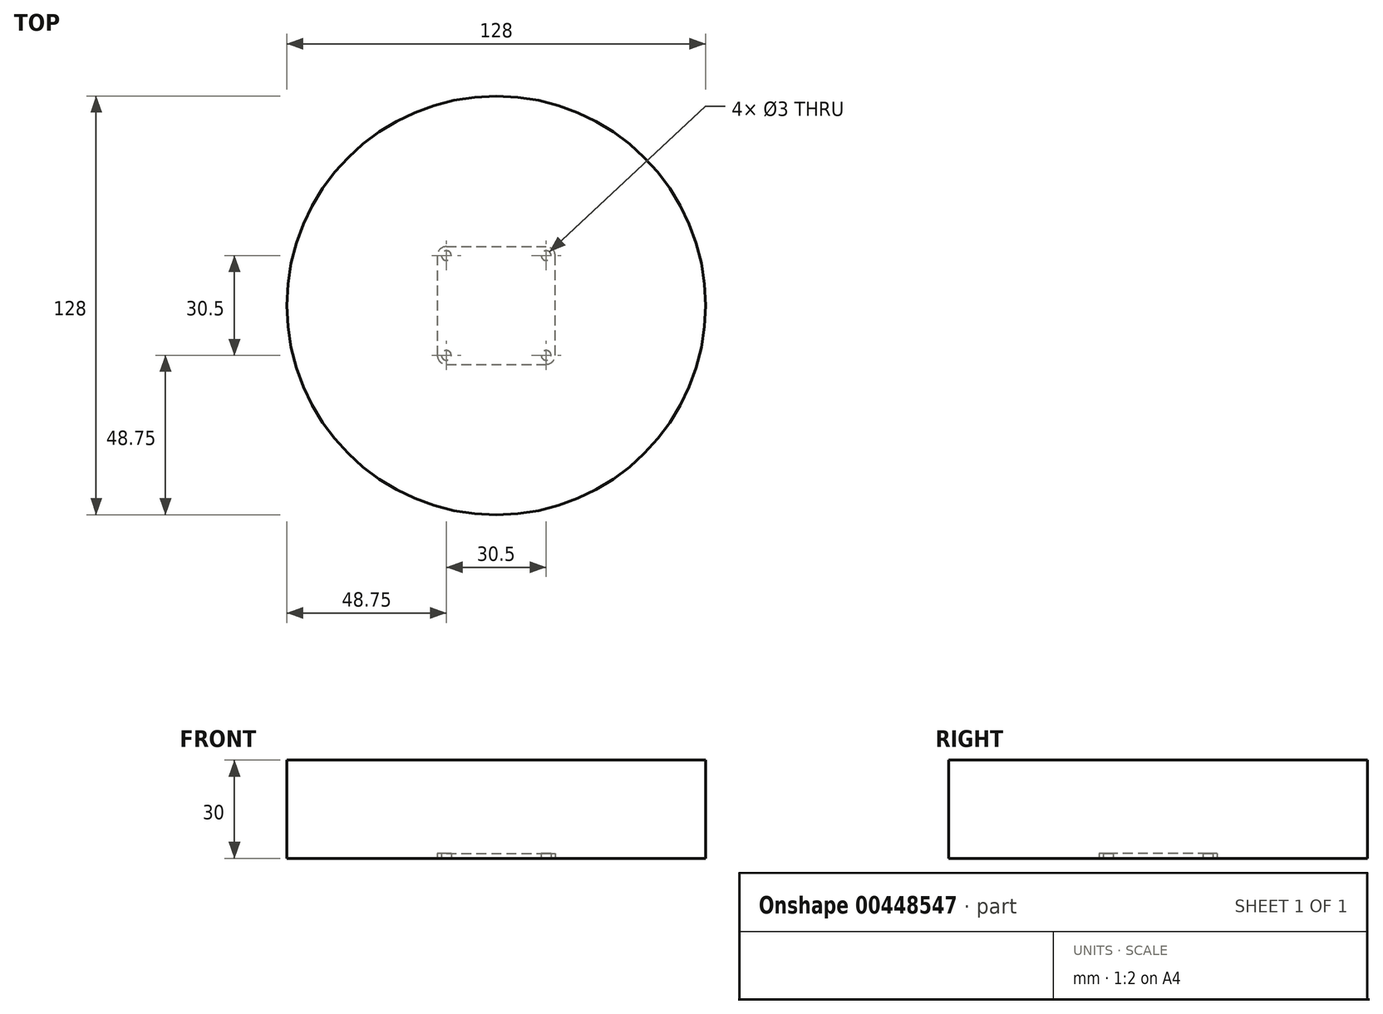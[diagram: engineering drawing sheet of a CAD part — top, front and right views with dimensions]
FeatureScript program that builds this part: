
annotation { "Feature Type Name" : "Feature", "Feature Type Description" : "" }
export const myFeature = defineFeature(function(context is Context, id is Id, definition is map)
    precondition{}
    {
        {
            var Q0;
            Q0=qCreatedBy(makeId("Top.planeOp"),FACE);
            var sketch = newSketch(context, id + "F0", { "sketchPlane" : qUnion([Q0])});
            skLineSegment(sketch, "E0.bottom", {"start": v(-15.25, 18) * mm, "end": v(0, 18) * mm});
            skLineSegment(sketch, "E0.left", {"start": v(-18, 15.25) * mm, "end": v(-18, 0) * mm});
            skCircle(sketch, "E1", {"center": v(-15.25, 15.25) * mm, "radius": 1.5 * mm});
            skLineSegment(sketch, "E2", {"start": v(0, 0) * mm, "end": v(0, 18) * mm, "construction": true});
            skLineSegment(sketch, "E3", {"start": v(0, 0) * mm, "end": v(-18, 0) * mm, "construction": true});
            skPoint(sketch, "E4.visualSharp", {"position": v(-18, 18) * mm});
            skArc(sketch, "E4.filletArc", {"start": v(-15.25, 18) * mm, "mid": v(-17.2, 17.2) * mm, "end": v(-18, 15.25) * mm});
            skCircle(sketch, "E5.MirrorC", {"center": v(15.25, 15.25) * mm, "radius": 1.5 * mm});
            skArc(sketch, "E6.MirrorCS", {"start": v(15.25, 18) * mm, "mid": v(17.2, 17.2) * mm, "end": v(18, 15.25) * mm});
            skPoint(sketch, "E7.MirrorP", {"position": v(18, 18) * mm});
            skLineSegment(sketch, "E8.MirrorCS", {"start": v(18, 15.25) * mm, "end": v(18, 0) * mm});
            skLineSegment(sketch, "E9.MirrorCS", {"start": v(15.25, 18) * mm, "end": v(0, 18) * mm});
            skLineSegment(sketch, "E10.MirrorCS", {"start": v(18, -15.25) * mm, "end": v(18, 0) * mm});
            skLineSegment(sketch, "E11.MirrorCS", {"start": v(-18, -15.25) * mm, "end": v(-18, 0) * mm});
            skArc(sketch, "E12.MirrorCS", {"start": v(-15.25, -18) * mm, "mid": v(-17.2, -17.2) * mm, "end": v(-18, -15.25) * mm});
            skArc(sketch, "E13.MirrorCS", {"start": v(15.25, -18) * mm, "mid": v(17.2, -17.2) * mm, "end": v(18, -15.25) * mm});
            skLineSegment(sketch, "E14.MirrorCS", {"start": v(-15.25, -18) * mm, "end": v(0, -18) * mm});
            skPoint(sketch, "E15.MirrorP", {"position": v(18, -18) * mm});
            skPoint(sketch, "E16.MirrorP", {"position": v(-18, -18) * mm});
            skCircle(sketch, "E17.MirrorC", {"center": v(-15.25, -15.25) * mm, "radius": 1.5 * mm});
            skCircle(sketch, "E18.MirrorC", {"center": v(15.25, -15.25) * mm, "radius": 1.5 * mm});
            skLineSegment(sketch, "E19.MirrorCS", {"start": v(15.25, -18) * mm, "end": v(0, -18) * mm});
            skSolve(sketch);
        }
        {
            var Q0;
            Q0=makeQuery(id+"F0.imprint","IMPRINT",FACE,{"disambiguationData":[TD([[makeQuery(id+"F0.imprint","IMPRINT",EDGE,{"derivedFrom":sQuery(id+"F0.wireOp",EDGE,"E0.bottom")}),-1.0]])]});
            extrude(context, id + "F1", {"entities" : qUnion([Q0]), "depth" : 1.5 * mm});
        }
        {
            var Q0;
            Q0=qCreatedBy(makeId("Top.planeOp"),FACE);
            var sketch = newSketch(context, id + "F2", { "sketchPlane" : qUnion([Q0])});
            skCircle(sketch, "E20", {"center": v(0, 0) * mm, "radius": 64 * mm});
            skSolve(sketch);
        }
        {
            var Q0;
            Q0 = qSketchRegion(id + "F2", true);
            extrude(context, id + "F3", {"entities" : qUnion([Q0]), "depth" : 30 * mm});
        }
    });
